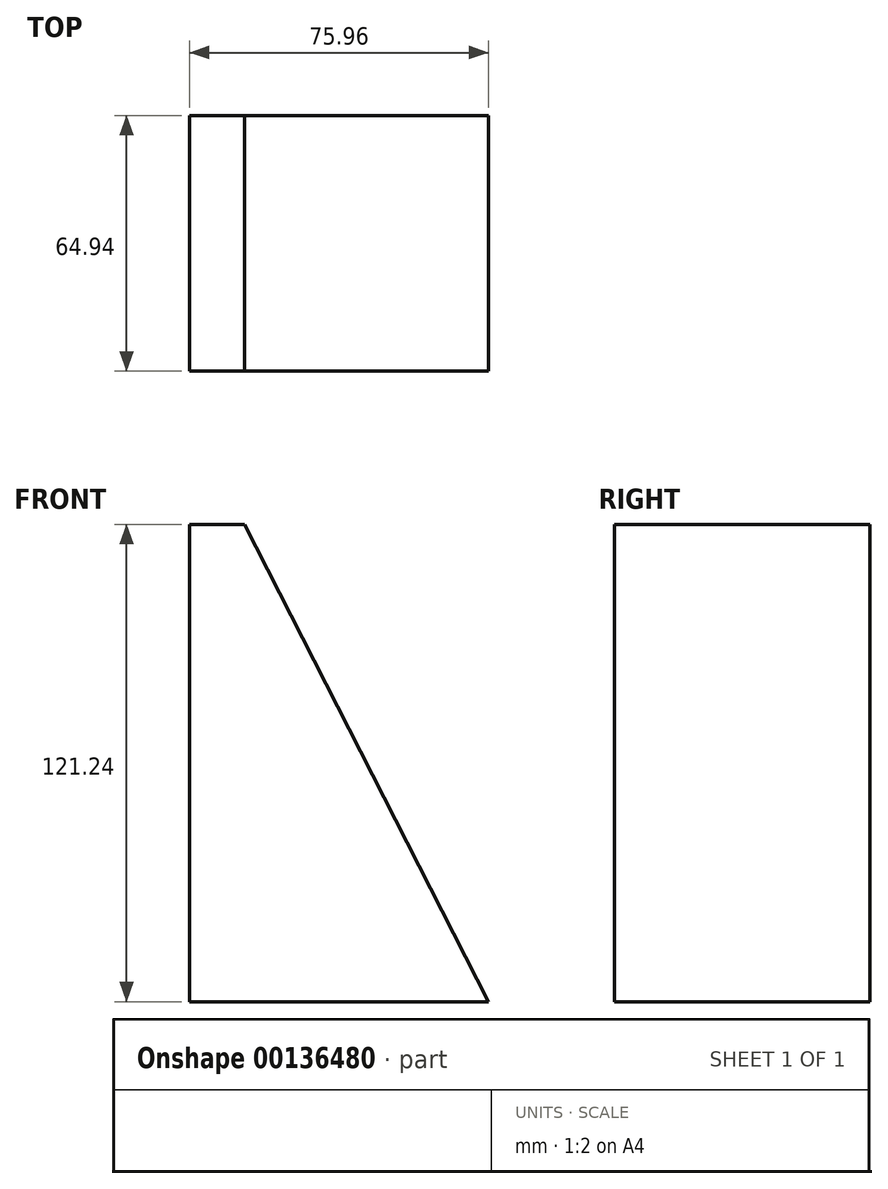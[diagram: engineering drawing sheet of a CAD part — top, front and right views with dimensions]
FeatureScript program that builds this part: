
annotation { "Feature Type Name" : "Feature", "Feature Type Description" : "" }
export const myFeature = defineFeature(function(context is Context, id is Id, definition is map)
    precondition{}
    {
        {
            var Q0;
            Q0=qCreatedBy(makeId("Front.planeOp"),FACE);
            var sketch = newSketch(context, id + "F0", { "sketchPlane" : qUnion([Q0])});
            skLineSegment(sketch, "E0", {"start": v(0, -55.32) * mm, "end": v(75.96, -55.32) * mm});
            skLineSegment(sketch, "E1", {"start": v(0, 65.92) * mm, "end": v(0, -55.32) * mm});
            skLineSegment(sketch, "E2", {"start": v(0, 65.92) * mm, "end": v(13.95, 65.92) * mm});
            skLineSegment(sketch, "E3", {"start": v(75.96, -55.32) * mm, "end": v(13.95, 65.92) * mm});
            skSolve(sketch);
        }
        {
            var Q0;
            Q0=makeQuery(id+"F0.imprint","IMPRINT",FACE,{"disambiguationData":[TD([[makeQuery(id+"F0.imprint","IMPRINT",EDGE,{"derivedFrom":sQuery(id+"F0.wireOp",EDGE,"E0")}),1.0]])]});
            var Q1;
            Q1=makeQuery(id+"FyOMqcvgZYDZvVN_0.imprint","IMPRINT",FACE,{"disambiguationData":[TD([[makeQuery(id+"FyOMqcvgZYDZvVN_0.imprint","IMPRINT",EDGE,{"derivedFrom":sQuery(id+"FyOMqcvgZYDZvVN_0.wireOp",EDGE,"C242ZKY3-sVDY-08BE-T7IM-WF1g2n84aYcW")}),-1.0]])]});
            extrude(context, id + "F1", {"entities" : qUnion([Q0, Q1]), "depth" : 24.65 * mm, "hasSecondDirection" : true, "secondDirectionOppositeDirection" : true, "secondDirectionDepth" : 40.3 * mm});
        }
    });
